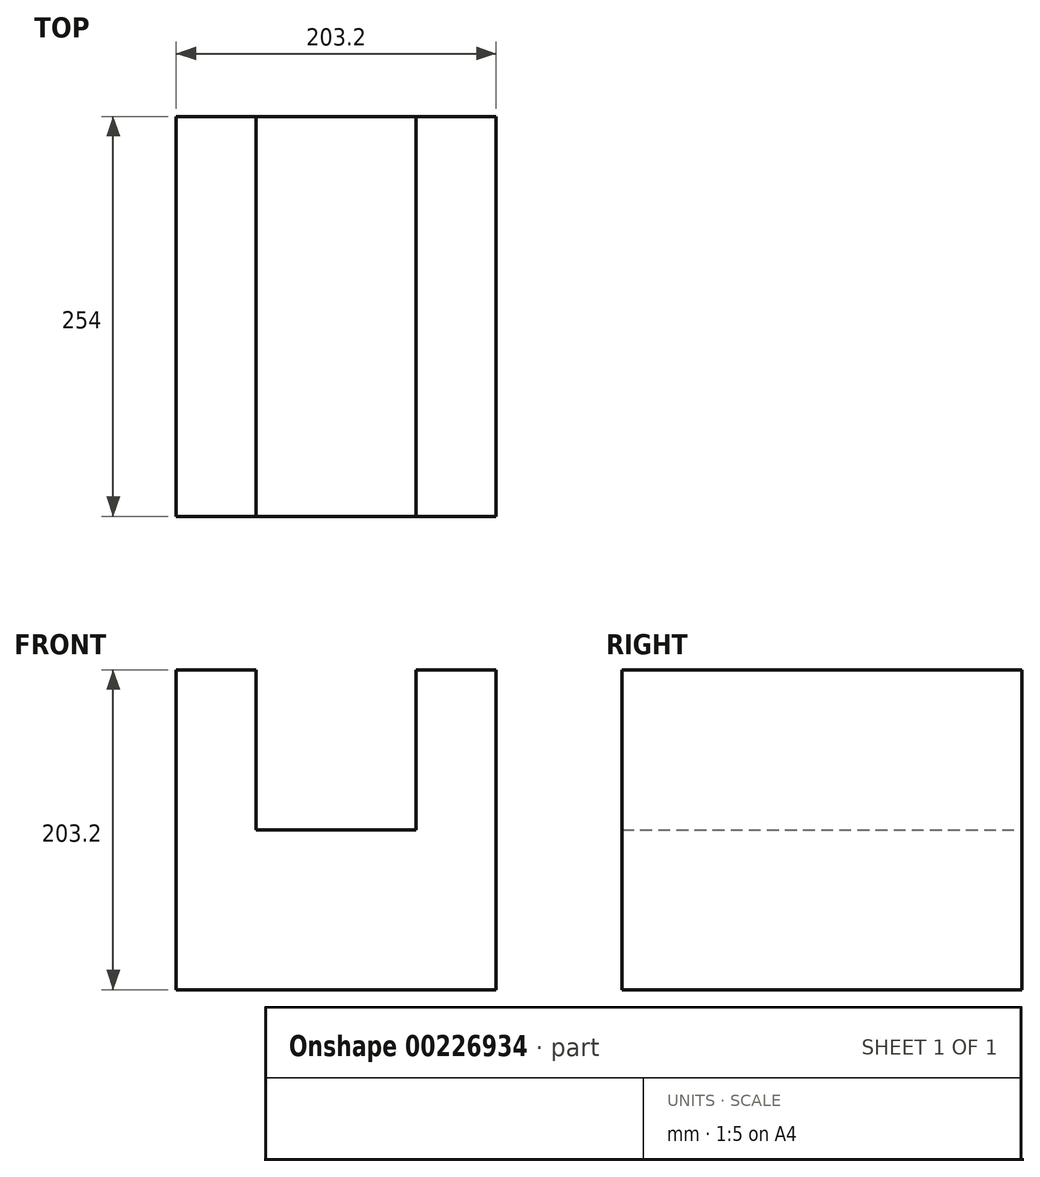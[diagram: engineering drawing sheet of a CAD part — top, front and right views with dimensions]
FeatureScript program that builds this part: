
annotation { "Feature Type Name" : "Feature", "Feature Type Description" : "" }
export const myFeature = defineFeature(function(context is Context, id is Id, definition is map)
    precondition{}
    {
        {
            var Q0;
            Q0=qCreatedBy(makeId("Front.planeOp"),FACE);
            var sketch = newSketch(context, id + "F0", { "sketchPlane" : qUnion([Q0])});
            skLineSegment(sketch, "E0.top", {"start": v(-98.3, -93.56) * mm, "end": v(104.9, -93.56) * mm});
            skLineSegment(sketch, "E0.left", {"start": v(-98.3, 109.64) * mm, "end": v(-98.3, -93.56) * mm});
            skLineSegment(sketch, "E0.right", {"start": v(104.9, 109.64) * mm, "end": v(104.9, -93.56) * mm});
            skLineSegment(sketch, "E1", {"start": v(-47.5, 109.64) * mm, "end": v(-47.5, 8.04) * mm});
            skLineSegment(sketch, "E2", {"start": v(-47.5, 8.04) * mm, "end": v(54.1, 8.04) * mm});
            skLineSegment(sketch, "E3", {"start": v(54.1, 8.04) * mm, "end": v(54.1, 109.64) * mm});
            skLineSegment(sketch, "E4", {"start": v(-98.3, 109.64) * mm, "end": v(-47.5, 109.64) * mm});
            skLineSegment(sketch, "E5", {"start": v(54.1, 109.64) * mm, "end": v(104.9, 109.64) * mm});
            skSolve(sketch);
        }
        {
            var Q0;
            Q0=makeQuery(id+"F0.imprint","IMPRINT",FACE,{"disambiguationData":[TD([[makeQuery(id+"F0.imprint","IMPRINT",EDGE,{"derivedFrom":sQuery(id+"F0.wireOp",EDGE,"E0.top")}),1.0]])]});
            extrude(context, id + "F1", {"entities" : qUnion([Q0]), "depth" : 254 * mm});
        }
    });
